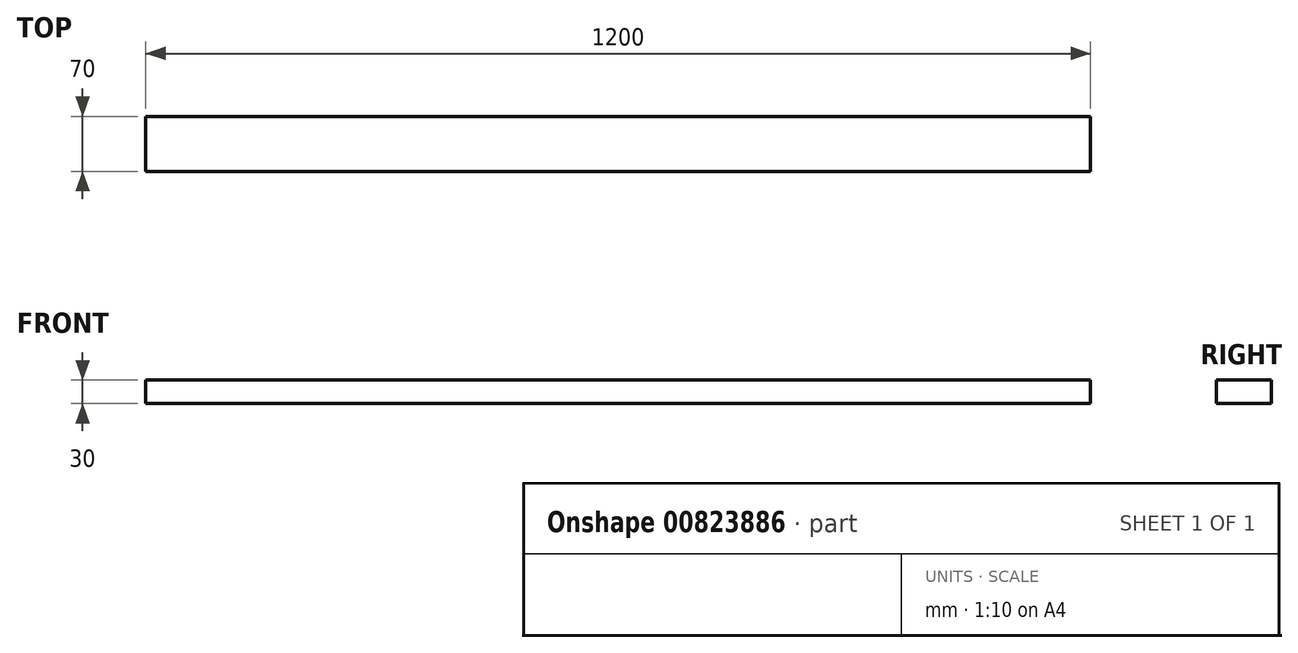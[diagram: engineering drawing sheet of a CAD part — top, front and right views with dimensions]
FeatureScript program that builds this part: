
annotation { "Feature Type Name" : "Feature", "Feature Type Description" : "" }
export const myFeature = defineFeature(function(context is Context, id is Id, definition is map)
    precondition{}
    {
        {
            var Q0;
            Q0=qCreatedBy(makeId("Right.planeOp"),FACE);
            var sketch = newSketch(context, id + "F0", { "sketchPlane" : qUnion([Q0])});
            skLineSegment(sketch, "E0.bottom", {"start": v(-35, 15) * mm, "end": v(35, 15) * mm});
            skLineSegment(sketch, "E0.top", {"start": v(-35, -15) * mm, "end": v(35, -15) * mm});
            skLineSegment(sketch, "E0.left", {"start": v(-35, 15) * mm, "end": v(-35, -15) * mm});
            skLineSegment(sketch, "E0.right", {"start": v(35, 15) * mm, "end": v(35, -15) * mm});
            skPoint(sketch, "E0.middle", {"position": v(0, 0) * mm});
            skSolve(sketch);
        }
        {
            var Q0;
            Q0=makeQuery(id+"F0.imprint","IMPRINT",FACE,{"disambiguationData":[TD([[makeQuery(id+"F0.imprint","IMPRINT",EDGE,{"derivedFrom":sQuery(id+"F0.wireOp",EDGE,"E0.bottom")}),-1.0]])]});
            extrude(context, id + "F1", {"entities" : qUnion([Q0]), "endBound" : BoundingType.SYMMETRIC, "depth" : 1200 * mm, "offsetDistance" : 25 * mm});
        }
    });
